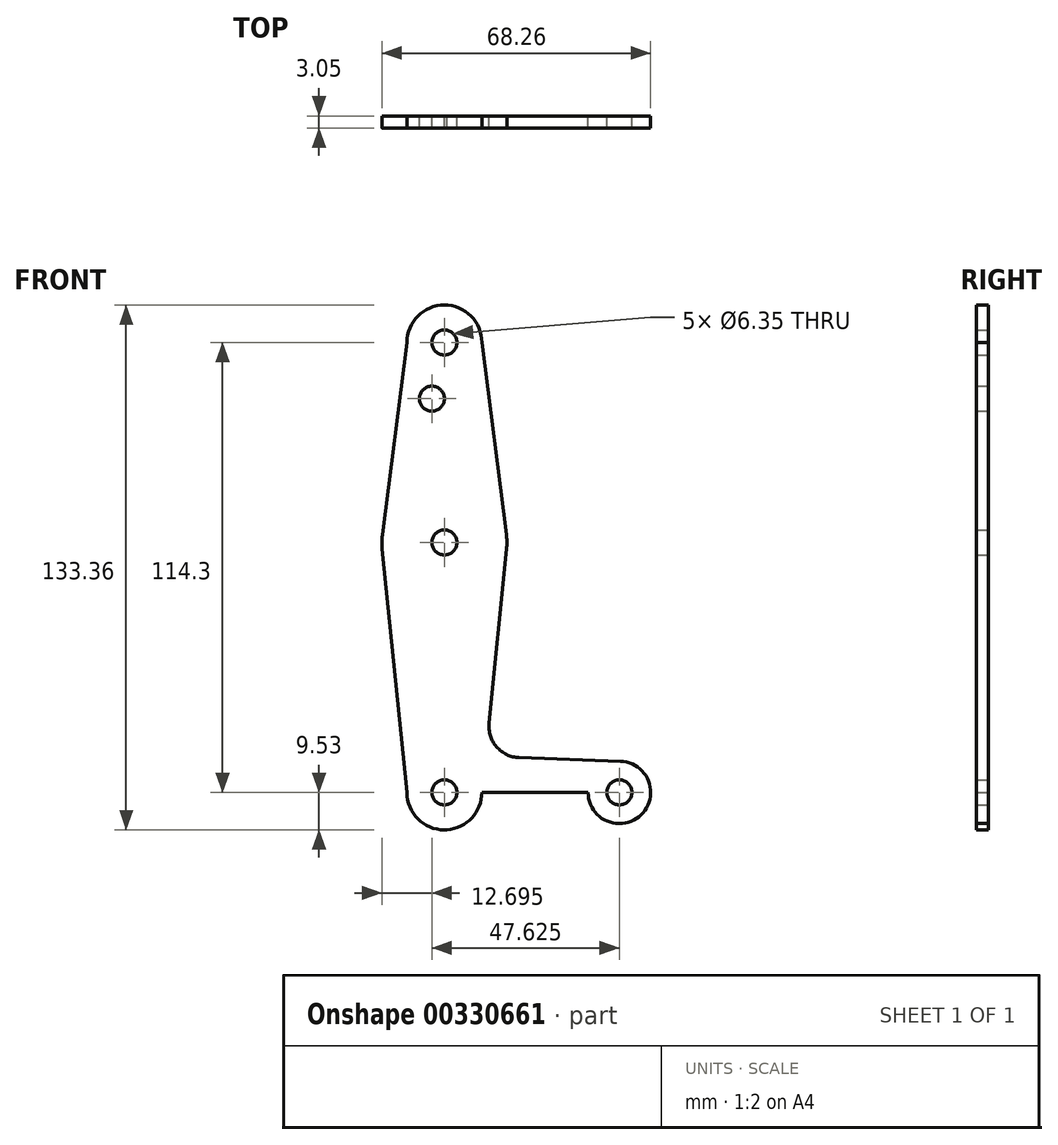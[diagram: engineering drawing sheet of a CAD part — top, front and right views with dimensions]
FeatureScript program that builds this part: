
annotation { "Feature Type Name" : "Feature", "Feature Type Description" : "" }
export const myFeature = defineFeature(function(context is Context, id is Id, definition is map)
    precondition{}
    {
        {
            var Q0;
            Q0=qCreatedBy(makeId("Front.planeOp"),FACE);
            var sketch = newSketch(context, id + "F0", { "sketchPlane" : qUnion([Q0])});
            skCircle(sketch, "E0", {"center": v(0, 114.3) * mm, "radius": 9.53 * mm});
            skLineSegment(sketch, "E1", {"start": v(0, 114.3) * mm, "end": v(0, 63.5) * mm});
            skCircle(sketch, "E2", {"center": v(0, 63.5) * mm, "radius": 15.88 * mm});
            skLineSegment(sketch, "E3", {"start": v(0, 63.5) * mm, "end": v(0, 0) * mm});
            skCircle(sketch, "E4", {"center": v(0, 0) * mm, "radius": 9.53 * mm});
            skLineSegment(sketch, "E5", {"start": v(0, 0) * mm, "end": v(44.45, 0) * mm});
            skCircle(sketch, "E6", {"center": v(44.45, 0) * mm, "radius": 7.94 * mm});
            skLineSegment(sketch, "E7", {"start": v(-9.52, 0) * mm, "end": v(-15.8, 61.9) * mm});
            skLineSegment(sketch, "E8", {"start": v(-9.53, 114.3) * mm, "end": v(-15.75, 65.5) * mm});
            skLineSegment(sketch, "E9", {"start": v(9.52, 114.3) * mm, "end": v(15.75, 65.5) * mm});
            skCircle(sketch, "E10", {"center": v(0, 63.5) * mm, "radius": 3.18 * mm});
            skCircle(sketch, "E11", {"center": v(44.45, 0) * mm, "radius": 3.18 * mm});
            skCircle(sketch, "E12", {"center": v(0, 114.3) * mm, "radius": 3.18 * mm});
            skCircle(sketch, "E13", {"center": v(0, 0) * mm, "radius": 3.18 * mm});
            skCircle(sketch, "E14", {"center": v(-3.18, 100.03) * mm, "radius": 3.18 * mm});
            skLineSegment(sketch, "E15", {"start": v(15.8, 61.9) * mm, "end": v(11.34, 17.59) * mm});
            skLineSegment(sketch, "E16", {"start": v(0, -9.53) * mm, "end": v(44.73, -7.93) * mm});
            skLineSegment(sketch, "E17", {"start": v(18.97, 8.85) * mm, "end": v(44.73, 7.93) * mm});
            skPoint(sketch, "E18.newPointA", {"position": v(9.57, 0) * mm});
            skPoint(sketch, "E18.newPointB", {"position": v(0, 9.52) * mm});
            skArc(sketch, "E18.filletArc", {"start": v(11.34, 17.59) * mm, "mid": v(13.26, 11.57) * mm, "end": v(18.97, 8.85) * mm});
            skSolve(sketch);
        }
        {
            var Q0;
            {var subQ10=sQuery(id+"F0.wireOp",EDGE,"E15");Q0=makeQuery(id+"F0.imprint","IMPRINT",FACE,{"disambiguationData":[TD([[makeQuery(id+"F0.imprint","IMPRINT",EDGE,{"derivedFrom":subQ10}),-1.0]])]});}
            var Q1;
            {var subQ0=sQuery(id+"F0.wireOp",EDGE,"E7");Q1=makeQuery(id+"F0.imprint","IMPRINT",FACE,{"disambiguationData":[TD([[makeQuery(id+"F0.imprint","IMPRINT",EDGE,{"derivedFrom":subQ0}),-1.0]])]});}
            var Q2;
            {var subQ0=sQuery(id+"F0.wireOp",EDGE,"E16");var subQ1=sQuery(id+"F0.wireOp",EDGE,"E4");var subQ2=makeQuery(id+"F0.imprint","INTERSECT",VERTEX,{"disambiguationData":[OD(1.0)],"derivedFrom":[subQ1,subQ0]});Q2=makeQuery(id+"F0.imprint","IMPRINT",FACE,{"disambiguationData":[TD([[makeQuery(id+"F0.imprint","IMPRINT",EDGE,{"disambiguationData":[TD([[subQ2,-1.0]])],"derivedFrom":subQ1}),-1.0]])]});}
            var Q3;
            Q3=makeQuery(id+"F0.imprint","IMPRINT",FACE,{"disambiguationData":[TD([[makeQuery(id+"F0.imprint","IMPRINT",EDGE,{"derivedFrom":sQuery(id+"F0.wireOp",EDGE,"E12")}),-1.0]])]});
            var Q4;
            {var subQ0=sQuery(id+"F0.wireOp",EDGE,"E2");var subQ3=sQuery(id+"F0.wireOp",EDGE,"E1");var subQ4=makeQuery(id+"F0.imprint","INTERSECT",VERTEX,{"derivedFrom":[subQ3,subQ0]});Q4=makeQuery(id+"F0.imprint","IMPRINT",FACE,{"disambiguationData":[TD([[makeQuery(id+"F0.imprint","IMPRINT",EDGE,{"disambiguationData":[TD([[subQ4,-1.0]])],"derivedFrom":subQ3}),-1.0]])]});}
            var Q5;
            {var subQ0=sQuery(id+"F0.wireOp",EDGE,"E9");Q5=makeQuery(id+"F0.imprint","IMPRINT",FACE,{"disambiguationData":[TD([[makeQuery(id+"F0.imprint","IMPRINT",EDGE,{"derivedFrom":subQ0}),-1.0]])]});}
            var Q6;
            {var subQ0=sQuery(id+"F0.wireOp",EDGE,"E4");var subQ1=sQuery(id+"F0.wireOp",EDGE,"E3");var subQ2=makeQuery(id+"F0.imprint","INTERSECT",VERTEX,{"derivedFrom":[subQ1,subQ0]});Q6=makeQuery(id+"F0.imprint","IMPRINT",FACE,{"disambiguationData":[TD([[makeQuery(id+"F0.imprint","IMPRINT",EDGE,{"disambiguationData":[TD([[subQ2,-1.0]])],"derivedFrom":subQ1}),1.0]])]});}
            var Q7;
            {var subQ1=sQuery(id+"F0.wireOp",EDGE,"E4");var subQ7=sQuery(id+"F0.wireOp",EDGE,"E3");var subQ8=makeQuery(id+"F0.imprint","INTERSECT",VERTEX,{"derivedFrom":[subQ7,subQ1]});Q7=makeQuery(id+"F0.imprint","IMPRINT",FACE,{"disambiguationData":[TD([[makeQuery(id+"F0.imprint","IMPRINT",EDGE,{"disambiguationData":[TD([[subQ8,-1.0]])],"derivedFrom":subQ7}),-1.0]])]});}
            var Q8;
            Q8=makeQuery(id+"F0.imprint","IMPRINT",FACE,{"disambiguationData":[TD([[makeQuery(id+"F0.imprint","IMPRINT",EDGE,{"derivedFrom":sQuery(id+"F0.wireOp",EDGE,"E11")}),-1.0]])]});
            var Q9;
            {var subQ0=sQuery(id+"F0.wireOp",EDGE,"E16");var subQ1=sQuery(id+"F0.wireOp",EDGE,"E4");var subQ2=makeQuery(id+"F0.imprint","INTERSECT",VERTEX,{"disambiguationData":[OD(0.0)],"derivedFrom":[subQ1,subQ0]});Q9=makeQuery(id+"F0.imprint","IMPRINT",FACE,{"disambiguationData":[TD([[makeQuery(id+"F0.imprint","IMPRINT",EDGE,{"disambiguationData":[TD([[subQ2,-1.0]])],"derivedFrom":subQ1}),1.0]])]});}
            var Q10;
            {var subQ0=sQuery(id+"F0.wireOp",EDGE,"E2");var subQ5=sQuery(id+"F0.wireOp",EDGE,"E1");var subQ9=makeQuery(id+"F0.imprint","INTERSECT",VERTEX,{"derivedFrom":[subQ5,subQ0]});Q10=makeQuery(id+"F0.imprint","IMPRINT",FACE,{"disambiguationData":[TD([[makeQuery(id+"F0.imprint","IMPRINT",EDGE,{"disambiguationData":[TD([[subQ9,-1.0]])],"derivedFrom":subQ5}),1.0]])]});}
            var Q11;
            {var subQ0=sQuery(id+"F0.wireOp",EDGE,"E8");Q11=makeQuery(id+"F0.imprint","IMPRINT",FACE,{"disambiguationData":[TD([[makeQuery(id+"F0.imprint","IMPRINT",EDGE,{"derivedFrom":subQ0}),1.0]])]});}
            extrude(context, id + "F1", {"entities" : qUnion([Q0, Q1, Q2, Q3, Q4, Q5, Q6, Q7, Q8, Q9, Q10, Q11]), "depth" : 3.05 * mm});
        }
    });
